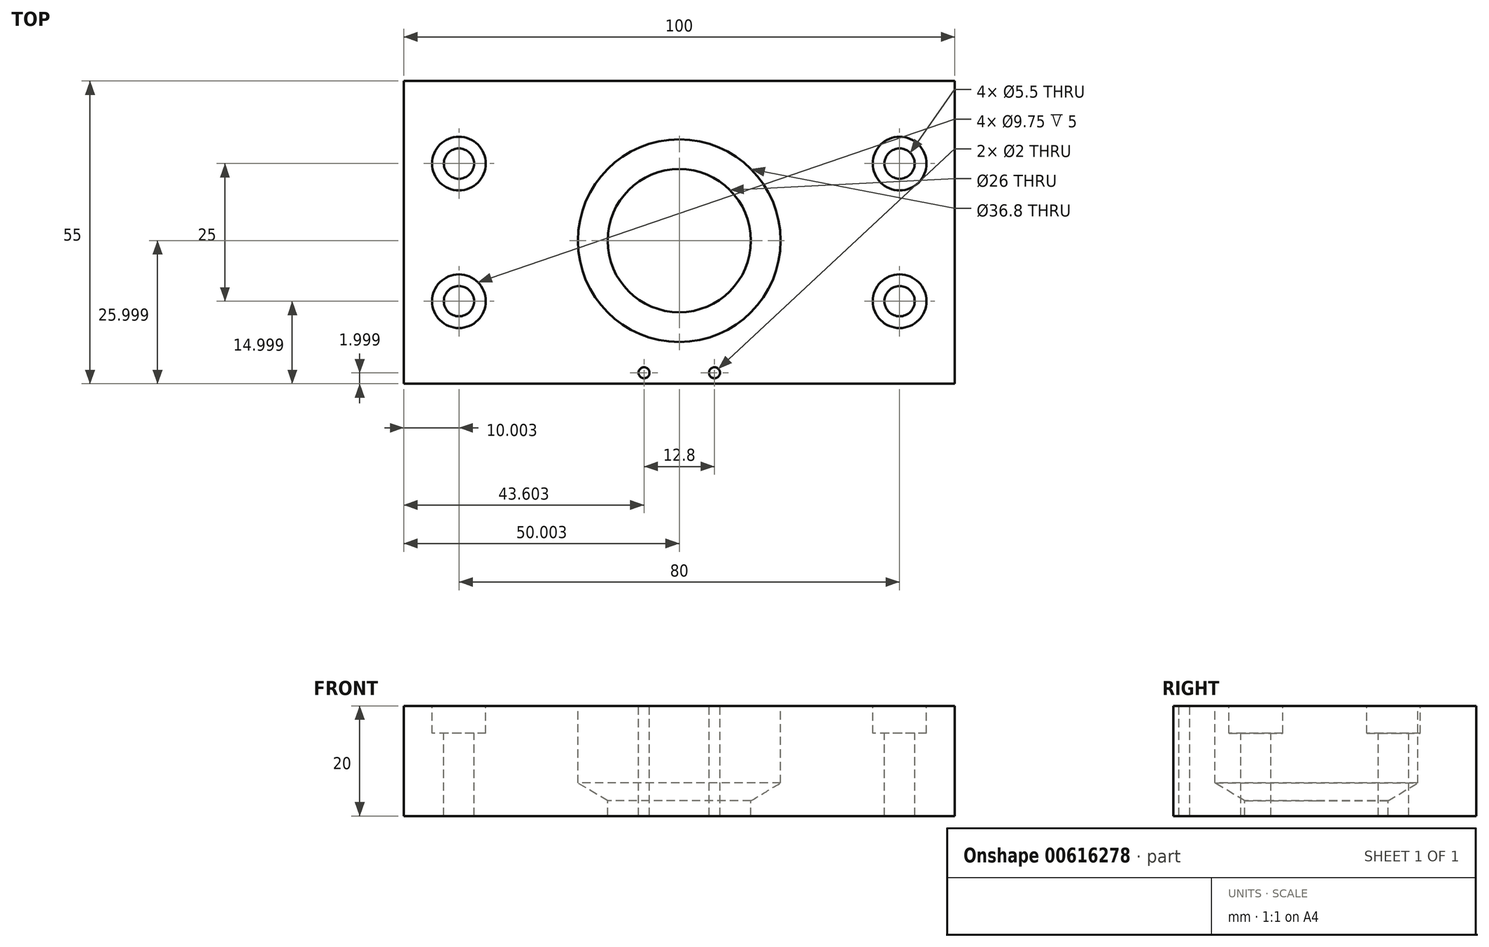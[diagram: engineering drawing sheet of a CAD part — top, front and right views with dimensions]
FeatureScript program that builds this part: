
annotation { "Feature Type Name" : "Feature", "Feature Type Description" : "" }
export const myFeature = defineFeature(function(context is Context, id is Id, definition is map)
    precondition{}
    {
        {
            var Q0;
            Q0=qCreatedBy(makeId("Top.planeOp"),FACE);
            var sketch = newSketch(context, id + "F0", { "sketchPlane" : qUnion([Q0])});
            skLineSegment(sketch, "E0.bottom", {"start": v(-52.29, 28.59) * mm, "end": v(47.71, 28.59) * mm});
            skLineSegment(sketch, "E0.top", {"start": v(-52.29, -26.41) * mm, "end": v(47.71, -26.41) * mm});
            skLineSegment(sketch, "E0.left", {"start": v(-52.29, 28.59) * mm, "end": v(-52.29, -26.41) * mm});
            skLineSegment(sketch, "E0.right", {"start": v(47.71, 28.59) * mm, "end": v(47.71, -26.41) * mm});
            skSolve(sketch);
        }
        {
            var Q0;
            Q0=makeQuery(id+"F0.imprint","IMPRINT",FACE,{"disambiguationData":[TD([[makeQuery(id+"F0.imprint","IMPRINT",EDGE,{"derivedFrom":sQuery(id+"F0.wireOp",EDGE,"E0.bottom")}),-1.0]])]});
            extrude(context, id + "F1", {"entities" : qUnion([Q0]), "depth" : 20 * mm, "offsetDistance" : 25 * mm});
        }
        {
            var Q0;
            Q0=makeQuery(id+"F1.opExtrude","CAP_FACE",FACE,{"disambiguationData":[OSD([sQuery(id+"F0.wireOp",EDGE,"E0.bottom"),sQuery(id+"F0.wireOp",EDGE,"E0.top"),sQuery(id+"F0.wireOp",EDGE,"E0.left"),sQuery(id+"F0.wireOp",EDGE,"E0.right")])],"isStart":false});
            var sketch = newSketch(context, id + "F2", { "sketchPlane" : qUnion([Q0])});
            skPoint(sketch, "E1", {"position": v(-2.29, -0.41) * mm});
            skSolve(sketch);
        }
        {
            var Q0;
            Q0=sQuery(id+"F2.wireOp",VERTEX,"E1");
            var Q1;
            Q1=makeQuery(id+"F1.opExtrude","SWEPT_BODY",BODY,{"disambiguationData":[OSD([sQuery(id+"F0.wireOp",EDGE,"E0.bottom"),sQuery(id+"F0.wireOp",EDGE,"E0.top"),sQuery(id+"F0.wireOp",EDGE,"E0.left"),sQuery(id+"F0.wireOp",EDGE,"E0.right")])]});
            hole(context, id + "F3", {"style" : HoleStyle.SIMPLE, "endStyle" : HoleEndStyle.THROUGH, "holeDiameter" : 26 * mm, "majorDiameter" : 5 * mm, "isTappedThrough" : true, "tappedDepth" : 17.9 * mm, "tapClearance" : 3, "locations" : qUnion([Q0]), "scope" : qUnion([Q1])});
        }
        {
            var Q0;
            Q0=sQuery(id+"F2.wireOp",VERTEX,"E1");
            var Q1;
            Q1=makeQuery(id+"F1.opExtrude","SWEPT_BODY",BODY,{"disambiguationData":[OSD([sQuery(id+"F0.wireOp",EDGE,"E0.bottom"),sQuery(id+"F0.wireOp",EDGE,"E0.top"),sQuery(id+"F0.wireOp",EDGE,"E0.left"),sQuery(id+"F0.wireOp",EDGE,"E0.right")])]});
            hole(context, id + "F4", {"style" : HoleStyle.SIMPLE, "endStyle" : HoleEndStyle.BLIND, "holeDiameter" : 36.8 * mm, "majorDiameter" : 5 * mm, "holeDepth" : 14 * mm, "isTappedThrough" : true, "tappedDepth" : 17.9 * mm, "tapClearance" : 3, "locations" : qUnion([Q0]), "scope" : qUnion([Q1])});
        }
        {
            var Q0;
            Q0=makeQuery(id+"F2.imprint","IMPRINT",FACE,{"disambiguationData":[TD([[makeQuery(id+"F2.imprint","IMPRINT",EDGE,{"derivedFrom":makeQuery(id+"F1.opExtrude","CAP_EDGE",EDGE,{"disambiguationData":[OSD([sQuery(id+"F0.wireOp",EDGE,"E0.bottom")])],"isStart":false})}),-1.0]])]});
            var sketch = newSketch(context, id + "F5", { "sketchPlane" : qUnion([Q0])});
            skPoint(sketch, "E2", {"position": v(-8.69, -24.41) * mm});
            skPoint(sketch, "E3", {"position": v(4.11, -24.41) * mm});
            skSolve(sketch);
        }
        {
            var Q0;
            Q0=sQuery(id+"F5.wireOp",VERTEX,"E2");
            var Q1;
            Q1=sQuery(id+"F5.wireOp",VERTEX,"E3");
            var Q2;
            Q2=makeQuery(id+"F1.opExtrude","SWEPT_BODY",BODY,{"disambiguationData":[OSD([sQuery(id+"F0.wireOp",EDGE,"E0.bottom"),sQuery(id+"F0.wireOp",EDGE,"E0.top"),sQuery(id+"F0.wireOp",EDGE,"E0.left"),sQuery(id+"F0.wireOp",EDGE,"E0.right")])]});
            hole(context, id + "F6", {"style" : HoleStyle.SIMPLE, "endStyle" : HoleEndStyle.THROUGH, "holeDiameter" : 2 * mm, "majorDiameter" : 5 * mm, "isTappedThrough" : true, "tappedDepth" : 17.9 * mm, "tapClearance" : 3, "locations" : qUnion([Q0, Q1]), "scope" : qUnion([Q2])});
        }
        {
            var Q0;
            Q0=makeQuery(id+"F2.imprint","IMPRINT",FACE,{"disambiguationData":[TD([[makeQuery(id+"F2.imprint","IMPRINT",EDGE,{"derivedFrom":makeQuery(id+"F1.opExtrude","CAP_EDGE",EDGE,{"disambiguationData":[OSD([sQuery(id+"F0.wireOp",EDGE,"E0.bottom")])],"isStart":false})}),-1.0]])]});
            var sketch = newSketch(context, id + "F7", { "sketchPlane" : qUnion([Q0])});
            skPoint(sketch, "E4", {"position": v(-42.29, -11.41) * mm});
            skPoint(sketch, "E5", {"position": v(-42.29, 13.59) * mm});
            skPoint(sketch, "E6", {"position": v(37.71, 13.59) * mm});
            skPoint(sketch, "E7", {"position": v(37.71, -11.41) * mm});
            skSolve(sketch);
        }
        {
            var Q0;
            Q0=sQuery(id+"F7.wireOp",VERTEX,"E5");
            var Q1;
            Q1=sQuery(id+"F7.wireOp",VERTEX,"E4");
            var Q2;
            Q2=sQuery(id+"F7.wireOp",VERTEX,"E7");
            var Q3;
            Q3=sQuery(id+"F7.wireOp",VERTEX,"E6");
            var Q4;
            Q4=makeQuery(id+"F1.opExtrude","SWEPT_BODY",BODY,{"disambiguationData":[OSD([sQuery(id+"F0.wireOp",EDGE,"E0.bottom"),sQuery(id+"F0.wireOp",EDGE,"E0.top"),sQuery(id+"F0.wireOp",EDGE,"E0.left"),sQuery(id+"F0.wireOp",EDGE,"E0.right")])]});
            hole(context, id + "F8", {"style" : HoleStyle.C_BORE, "endStyle" : HoleEndStyle.THROUGH, "standardTappedOrClearance" : lookupTablePath({ "standard" : "ISO", "fit" : "Normal", "size" : "M5", "type" : "Clearance" }), "standardBlindInLast" : lookupTablePath({ "fit" : "Standard", "standard" : "ISO", "size" : "M5", "type" : "Clearance" }), "holeDiameter" : 5.5 * mm, "cBoreDiameter" : 9.75 * mm, "cBoreDepth" : 5 * mm, "majorDiameter" : 5 * mm, "isTappedThrough" : true, "tappedDepth" : 17.9 * mm, "tapClearance" : 3, "locations" : qUnion([Q0, Q1, Q2, Q3]), "scope" : qUnion([Q4])});
        }
    });
